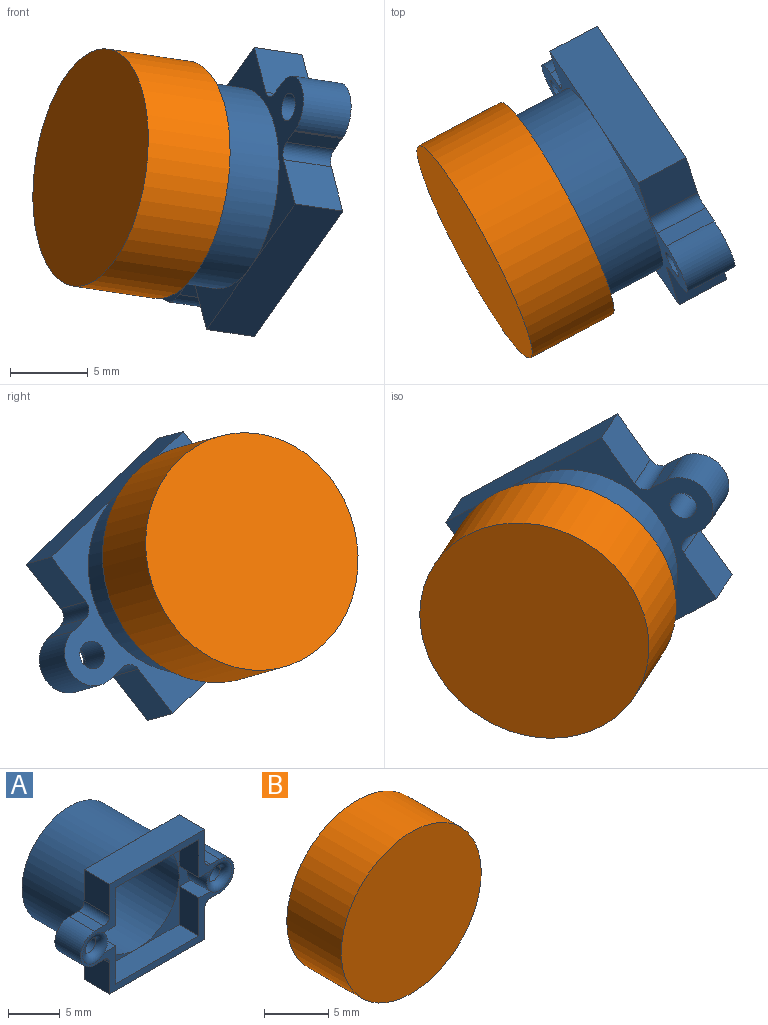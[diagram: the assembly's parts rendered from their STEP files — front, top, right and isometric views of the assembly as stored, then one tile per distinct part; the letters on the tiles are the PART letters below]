
ASSEMBLY  parts=2 mates=1
PART A: 43 faces, bbox 21.9x12x13 mm
  f0: cylinder r=5.5mm len=11mm, axis (0,1,0), area 27.6mm2, adj f12,f31
  f1: plane 3.72x3.5mm, normal (1,0,0), area 13mm2, adj f15,f17,f20,f41
  f2: plane 3.68x3.5mm, normal (-1,0,0), area 12.9mm2, adj f13,f17,f21,f39
  f3: cylinder r=2mm len=4mm, axis (0,1,0), area 21.7mm2, adj f4,f10,f17,f21
  f4: plane 3.5x0.09mm, normal (0,0,-1), area 0.3mm2, adj f3,f5,f17,f21
  f5: plane 3.5x1.14mm, normal (0.02,0,-1), area 4mm2, adj f4,f17,f21,f39
  f6: plane 3.5x1.14mm, normal (-0.02,0,-1), area 4mm2, adj f7,f17,f20,f40
  f7: cylinder r=2mm len=4mm, axis (0,1,0), area 22mm2, adj f6,f8,f17,f20
  f8: plane 3.5x1.26mm, normal (0.02,0,1), area 4.4mm2, adj f7,f17,f20,f41
  f9: cylinder r=0.9mm len=2.7mm, axis (0,1,0), area 15.3mm2, adj f18,f21
  f10: plane 3.5x1.26mm, normal (-0.02,0,1), area 4.4mm2, adj f3,f17,f21,f42
  f11: cylinder r=0.9mm len=2.7mm, axis (0,1,0), area 15.3mm2, adj f19,f20
  f12: plane 13x13mm, normal (0,1,0), area 37.7mm2, adj f0,f22
  f13: plane 13x3.5mm, normal (0,0,-1), area 45.5mm2, adj f2,f14,f17,f20,f21
  f14: plane 3.68x3.5mm, normal (1,0,0), area 12.9mm2, adj f13,f17,f20,f40
  f15: plane 13x3.5mm, normal (0,0,1), area 45.5mm2, adj f1,f16,f17,f20,f21
  f16: plane 3.72x3.5mm, normal (-1,0,0), area 13mm2, adj f15,f17,f21,f42
  f17: plane 21x13mm, normal (0,-1,0), area 44mm2, adj f1,f2,f3,f4,f5,f6,f7,f8
  f18: torus R=1.7mm, axis (0,-1,0), area 9.4mm2, adj f9,f17,f28
  f19: torus R=1.7mm, axis (0,-1,0), area 9.4mm2, adj f11,f17,f30
  f20: plane 13x10.5mm, normal (0,1,0), area 30.1mm2, adj f1,f6,f7,f8,f11,f13,f14,f15
  f21: plane 13x10.5mm, normal (0,1,0), area 30.1mm2, adj f2,f3,f4,f5,f9,f10,f13,f15
  f22: cylinder r=6.5mm len=13mm, axis (0,1,0), area 347.1mm2, adj f12,f20,f21
  f23: plane 4.48x2.7mm, normal (-1,0,0), area 12.1mm2, adj f17,f27,f34,f36
  f24: plane 4.52x2.7mm, normal (1,0,0), area 12.2mm2, adj f17,f25,f32,f37
  f25: plane 2.7x1.57mm, normal (-0.02,0,1), area 4.2mm2, adj f17,f24,f28,f37
  f26: plane 2.7x1.57mm, normal (0.02,0,1), area 4.2mm2, adj f17,f30,f33,f36
  f27: plane 2.7x1.62mm, normal (-0.02,0,-1), area 4.4mm2, adj f17,f23,f30,f36
  f28: cylinder r=1.7mm len=2.7mm, axis (0,1,0), area 7.2mm2, adj f18,f25,f29,f37
  f29: plane 2.7x1.62mm, normal (0.02,0,-1), area 4.4mm2, adj f17,f28,f35,f37
  f30: cylinder r=1.7mm len=2.7mm, axis (0,1,0), area 7.2mm2, adj f19,f26,f27,f36
  f31: plane 11.4x11.4mm, normal (0,-1,0), area 7mm2, adj f0,f38
  f32: plane 11.4x2.7mm, normal (0,0,1), area 30.8mm2, adj f17,f24,f33,f36,f37
  f33: plane 4.52x2.7mm, normal (-1,0,0), area 12.2mm2, adj f17,f26,f32,f36
  f34: plane 11.4x2.7mm, normal (0,0,-1), area 30.8mm2, adj f17,f23,f35,f36,f37
  f35: plane 4.48x2.7mm, normal (1,0,0), area 12.1mm2, adj f17,f29,f34,f37
  f36: plane 11.4x7.32mm, normal (0,-1,0), area 17mm2, adj f23,f26,f27,f30,f32,f33,f34,f38
  f37: plane 11.4x7.32mm, normal (0,-1,0), area 17mm2, adj f24,f25,f28,f29,f32,f34,f35,f38
  f38: cylinder r=5.7mm len=11.4mm, axis (0,1,0), area 304.4mm2, adj f31,f36,f37
  f39: cylinder r=0.8mm len=3.5mm, axis (0,-1,0), area 4.5mm2, adj f2,f5,f17,f21
  f40: cylinder r=0.8mm len=3.5mm, axis (0,-1,0), area 4.5mm2, adj f6,f14,f17,f20
  f41: cylinder r=0.8mm len=3.5mm, axis (0,1,0), area 4.3mm2, adj f1,f8,f17,f20
  f42: cylinder r=0.8mm len=3.5mm, axis (0,1,0), area 4.3mm2, adj f10,f16,f17,f21
PART B: 5 faces, bbox 15.4x6x15.4 mm
  f0: cylinder r=7.7mm len=15.4mm, axis (0,1,0), area 290.3mm2, adj f1,f2
  f1: plane 15.4x15.4mm, normal (0,-1,0), area 186.3mm2, adj f0
  f2: plane 15.4x15.4mm, normal (0,1,0), area 45.2mm2, adj f0,f3
  f3: cylinder r=6.7mm len=13.4mm, axis (0,1,0), area 210.5mm2, adj f2,f4
  f4: plane 13.4x13.4mm, normal (0,1,0), area 141mm2, adj f3
PLACE A rot(axis=(-0.28,0.25,0.92),124.3deg) t=(21.53,-37.31,1.89)mm
PLACE B rot(axis=(-0.39,-0.44,-0.81),70.3deg) t=(25.26,-35.34,1.34)mm
MATE parallel A.f22 <-> B.f0  axis (-0.88,-0.46,0.13) through (25.26,-35.34,1.34)mm
